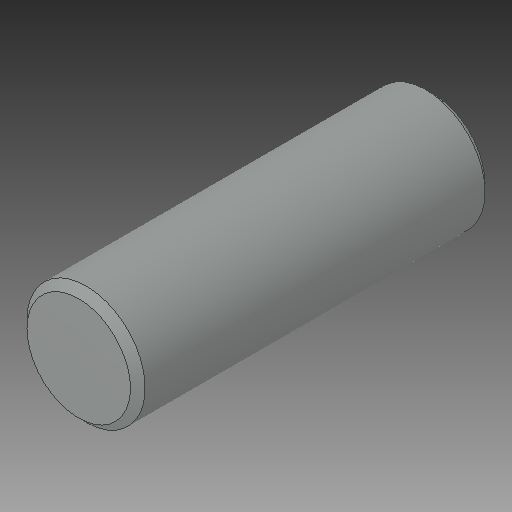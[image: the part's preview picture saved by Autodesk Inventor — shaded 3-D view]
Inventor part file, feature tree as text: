
AUTODESK INVENTOR PART (.ipt)
format: ipt  version: 2017 SP1 (Build 210196100, 196)  size: 97,792 bytes
history: native  units: in
note: dims shown in document units (in); Inventor stores cm internally (conversion verified against a paired STEP export)
features: chamfer x1
ambient origin geometry x8: Origin, YZ Plane, XZ Plane, XY Plane, X Axis, Y Axis, Z Axis, Center Point
bodies: Solid1 (feature_tree)
feature tree (1):
  chamfer  "Chamfer1"  [1 undecoded]
note: 1 required parameter value undecoded (feature->parameter linkage not recoverable at this tier; creation-order binding heuristic only, values carry confidence <= 0.55)
